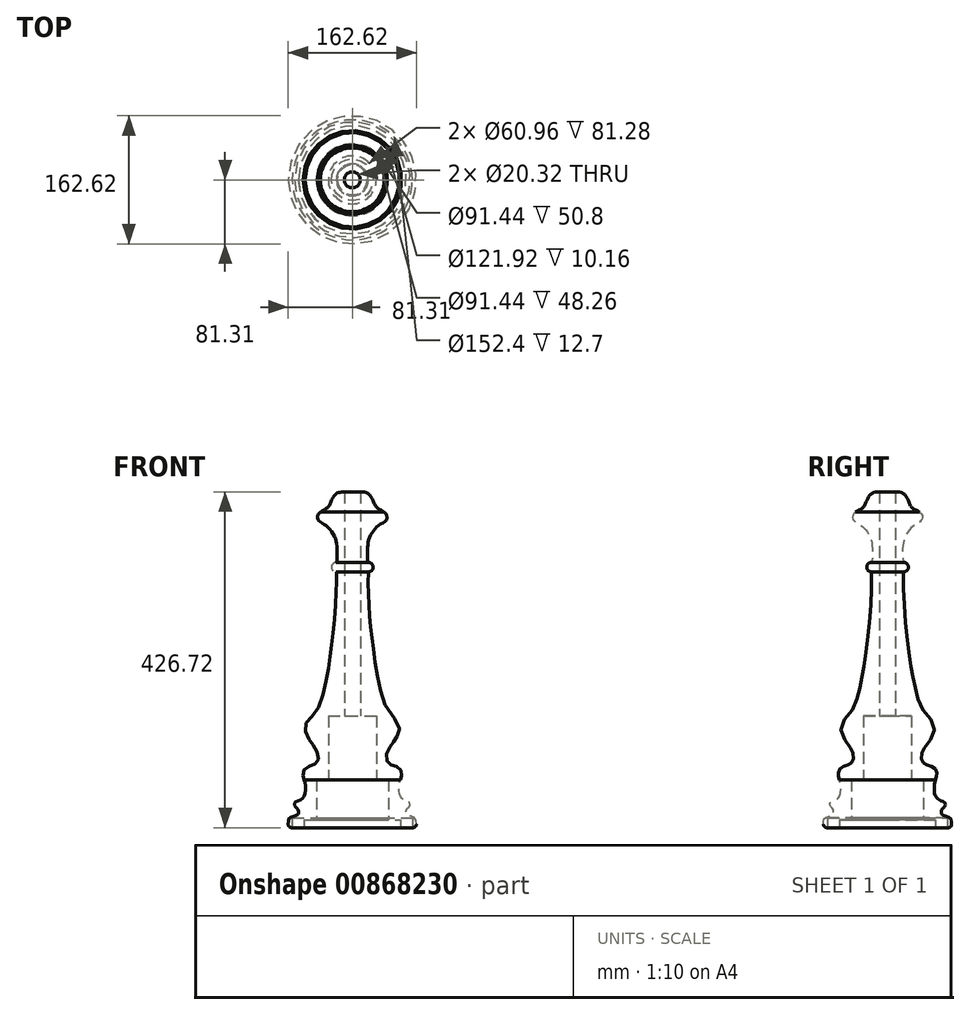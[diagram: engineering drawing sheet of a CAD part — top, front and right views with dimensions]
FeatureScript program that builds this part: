
annotation { "Feature Type Name" : "Feature", "Feature Type Description" : "" }
export const myFeature = defineFeature(function(context is Context, id is Id, definition is map)
    precondition{}
    {
        {
            var Q0;
            Q0=qCreatedBy(makeId("Front.planeOp"),FACE);
            var sketch = newSketch(context, id + "F0", { "sketchPlane" : qUnion([Q0])});
            skLineSegment(sketch, "E0", {"start": v(0, 0) * mm, "end": v(0, 533.4) * mm, "construction": true});
            skLineSegment(sketch, "E1", {"start": v(0, 533.4) * mm, "end": v(-12.7, 533.4) * mm, "construction": true});
            skLineSegment(sketch, "E2", {"start": v(0, 0) * mm, "end": v(-57.15, 0) * mm, "construction": true});
            skLineSegment(sketch, "E3", {"start": v(0, 0) * mm, "end": v(0, 76.2) * mm, "construction": true});
            skLineSegment(sketch, "E4", {"start": v(0, 76.2) * mm, "end": v(0, 254) * mm, "construction": true});
            skLineSegment(sketch, "E5", {"start": v(0, 254) * mm, "end": v(0, 406.4) * mm, "construction": true});
            skLineSegment(sketch, "E6", {"start": v(0, 406.4) * mm, "end": v(0, 533.4) * mm, "construction": true});
            skLineSegment(sketch, "E7", {"start": v(0, 76.2) * mm, "end": v(-38.1, 76.2) * mm, "construction": true});
            skLineSegment(sketch, "E8", {"start": v(0, 254) * mm, "end": v(-12.7, 254) * mm, "construction": true});
            skLineSegment(sketch, "E9", {"start": v(0, 406.4) * mm, "end": v(-25.4, 406.4) * mm, "construction": true});
            skLineSegment(sketch, "E10", {"start": v(0, 0) * mm, "end": v(-101.6, 0) * mm, "construction": true});
            skLineSegment(sketch, "E11", {"start": v(0, 76.2) * mm, "end": v(-76.2, 76.2) * mm, "construction": true});
            skLineSegment(sketch, "E12", {"start": v(0, 254) * mm, "end": v(-38.1, 254) * mm, "construction": true});
            skLineSegment(sketch, "E13", {"start": v(0, 533.4) * mm, "end": v(-50.8, 533.4) * mm});
            skArc(sketch, "E14", {"start": v(-25.29, 421.2) * mm, "mid": v(-33.07, 413.86) * mm, "end": v(-25.4, 406.4) * mm});
            skFitSpline(sketch, "E15", {"points": [v(-25.29, 421.2) * mm, v(-24.38, 446.96) * mm, v(-28.45, 463) * mm, v(-40, 478.41) * mm, v(-50.77, 485.39) * mm, v(-55.09, 490.6) * mm, v(-50.77, 501.12) * mm], "startDerivative": vector(24.16, 100.9) * mm, "endDerivative": vector(103.99, 86.78) * mm});
            skFitSpline(sketch, "E16", {"points": [v(-76.2, 76.2) * mm, v(-74.53, 54.97) * mm, v(-81.64, 44.37) * mm, v(-91.2, 39.28) * mm, v(-90.58, 33.57) * mm, v(-86.23, 28.97) * mm, v(-85.73, 24.38) * mm, v(-86.6, 20.78) * mm, v(-98.4, 16.18) * mm, v(-101.6, 0) * mm], "startDerivative": vector(23.07, -83.97) * mm, "endDerivative": vector(0.6, -226.71) * mm});
            skLineSegment(sketch, "E17", {"start": v(-101.6, 0) * mm, "end": v(-57.15, 0) * mm});
            skLineSegment(sketch, "E18", {"start": v(-57.15, 0) * mm, "end": v(-57.15, 76.2) * mm});
            skLineSegment(sketch, "E19", {"start": v(-57.15, 76.2) * mm, "end": v(-38.1, 76.2) * mm});
            skLineSegment(sketch, "E20", {"start": v(-38.1, 76.2) * mm, "end": v(-38.1, 177.8) * mm});
            skLineSegment(sketch, "E21", {"start": v(-38.1, 177.8) * mm, "end": v(-12.7, 177.8) * mm});
            skLineSegment(sketch, "E22", {"start": v(-12.7, 177.8) * mm, "end": v(-12.7, 533.4) * mm});
            skFitSpline(sketch, "E23", {"points": [v(-25.4, 406.4) * mm, v(-25.4, 375.85) * mm, v(-29.02, 320.52) * mm, v(-34.53, 275.92) * mm, v(-41.92, 231.75) * mm, v(-59.38, 181.62) * mm, v(-74.35, 163.27) * mm, v(-69.17, 141.63) * mm, v(-60.7, 129.87) * mm, v(-53.65, 112.47) * mm, v(-58.35, 101.65) * mm, v(-68.94, 97.61) * mm, v(-77.4, 90.7) * mm, v(-77.64, 81.43) * mm, v(-76.2, 76.2) * mm], "startDerivative": vector(9.7, -407) * mm, "endDerivative": vector(55.45, -136.1) * mm});
            skPoint(sketch, "E24.1.internal.snap0", {"position": v(-25.4, 533.4) * mm});
            skFitSpline(sketch, "E24", {"points": [v(-12.7, 533.4) * mm, v(-25.4, 530.46) * mm, v(-33.25, 518.84) * mm, v(-38.52, 508.67) * mm, v(-50.77, 501.12) * mm], "startDerivative": vector(-54.58, -3.25) * mm, "endDerivative": vector(-75.94, -49.56) * mm});
            skSolve(sketch);
        }
        {
            var Q0;
            Q0=qSketchRegion(id+"F0",true);
            var Q1;
            Q1=sQuery(id+"F0.wireOp",EDGE,"E5");
            revolve(context, id + "F1", {"surfaceOperationType" : NewSurfaceOperationType.NEW, "entities" : qUnion([Q0]), "axis" : qUnion([Q1]), "revolveType" : RevolveType.FULL});
        }
        {
            var Q0;
            Q0=makeQuery(id+"F1.opRevolve","SWEPT_EDGE",EDGE,{"disambiguationData":[OSD([sQuery(id+"F0.wireOp",EDGE,"E16"),sQuery(id+"F0.wireOp",EDGE,"E17")])]});
            fillet(context, id + "F2", {"entities" : qUnion([Q0]), "radius" : 5.08 * mm, "tangentPropagation" : true, "allowEdgeOverflow" : false});
        }
        {
            var Q0;
            Q0=makeQuery(id+"F1.opRevolve","SWEPT_FACE",FACE,{"disambiguationData":[OSD([sQuery(id+"F0.wireOp",EDGE,"E17")])]});
            var sketch = newSketch(context, id + "F3", { "sketchPlane" : qUnion([Q0])});
            skCircle(sketch, "E25", {"center": v(0, 0) * mm, "radius": 76.2 * mm});
            skSolve(sketch);
        }
        {
            var Q0;
            Q0=qSketchRegion(id+"F3",true);
            extrude(context, id + "F4", {"entities" : qUnion([Q0]), "operationType" : NewBodyOperationType.REMOVE, "oppositeDirection" : true, "depth" : 12.7 * mm, "offsetDistance" : 25.4 * mm});
        }
        {
            var Q0;
            Q0=makeQuery(id+"F1.opRevolve","SWEPT_BODY",BODY,{"disambiguationData":[OSD([sQuery(id+"F0.wireOp",EDGE,"E14"),sQuery(id+"F0.wireOp",EDGE,"E15"),sQuery(id+"F0.wireOp",EDGE,"E16"),sQuery(id+"F0.wireOp",EDGE,"E17"),sQuery(id+"F0.wireOp",EDGE,"E18"),sQuery(id+"F0.wireOp",EDGE,"E19"),sQuery(id+"F0.wireOp",EDGE,"E20"),sQuery(id+"F0.wireOp",EDGE,"E21"),sQuery(id+"F0.wireOp",EDGE,"E22"),sQuery(id+"F0.wireOp",EDGE,"E23"),sQuery(id+"F0.wireOp",EDGE,"E24")])]});
            var Q1;
            Q1=qCreatedBy(makeId("Origin.pointOp"),VERTEX);
            transform(context, id + "F5", {"entities" : qUnion([Q0]), "transformType" : TransformType.SCALE_UNIFORMLY, "scale" : .8, "scalePoint" : qUnion([Q1]), "makeCopy" : false});
        }
    });
